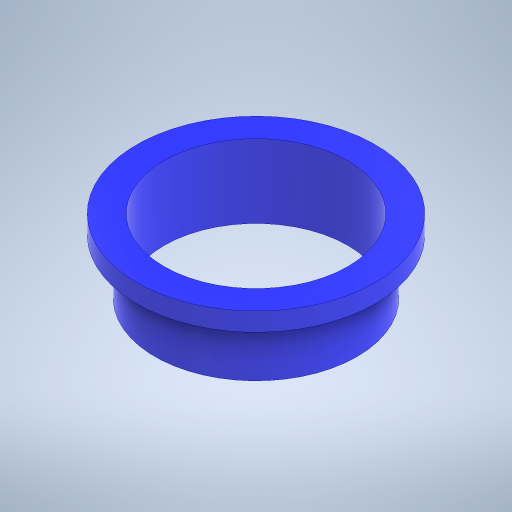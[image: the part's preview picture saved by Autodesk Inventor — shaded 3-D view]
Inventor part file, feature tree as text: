
AUTODESK INVENTOR PART (.ipt)
format: ipt  version: 2024 (Build 280153000, 153)  size: 261,120 bytes
history: native  units: mm
features: extrude x2, other x1, sketch x1
ambient origin geometry x8: Origin, YZ Plane, XZ Plane, XY Plane, X Axis, Y Axis, Z Axis, Center Point
bodies: Solid1 (feature_tree)
feature tree (4):
  extrude  "Extrusion1"  Depth=1.0mm
  extrude  "Extrusion2"  Depth=3.0mm TaperAngle=0.0deg
  other  "Work Point1"
  sketch  "Sketch2"  dims[d0=10.0mm d1=11.0mm d2=3.0mm d3=0.0mm d4=13.0mm d5=1.0mm d6=0.0mm]
